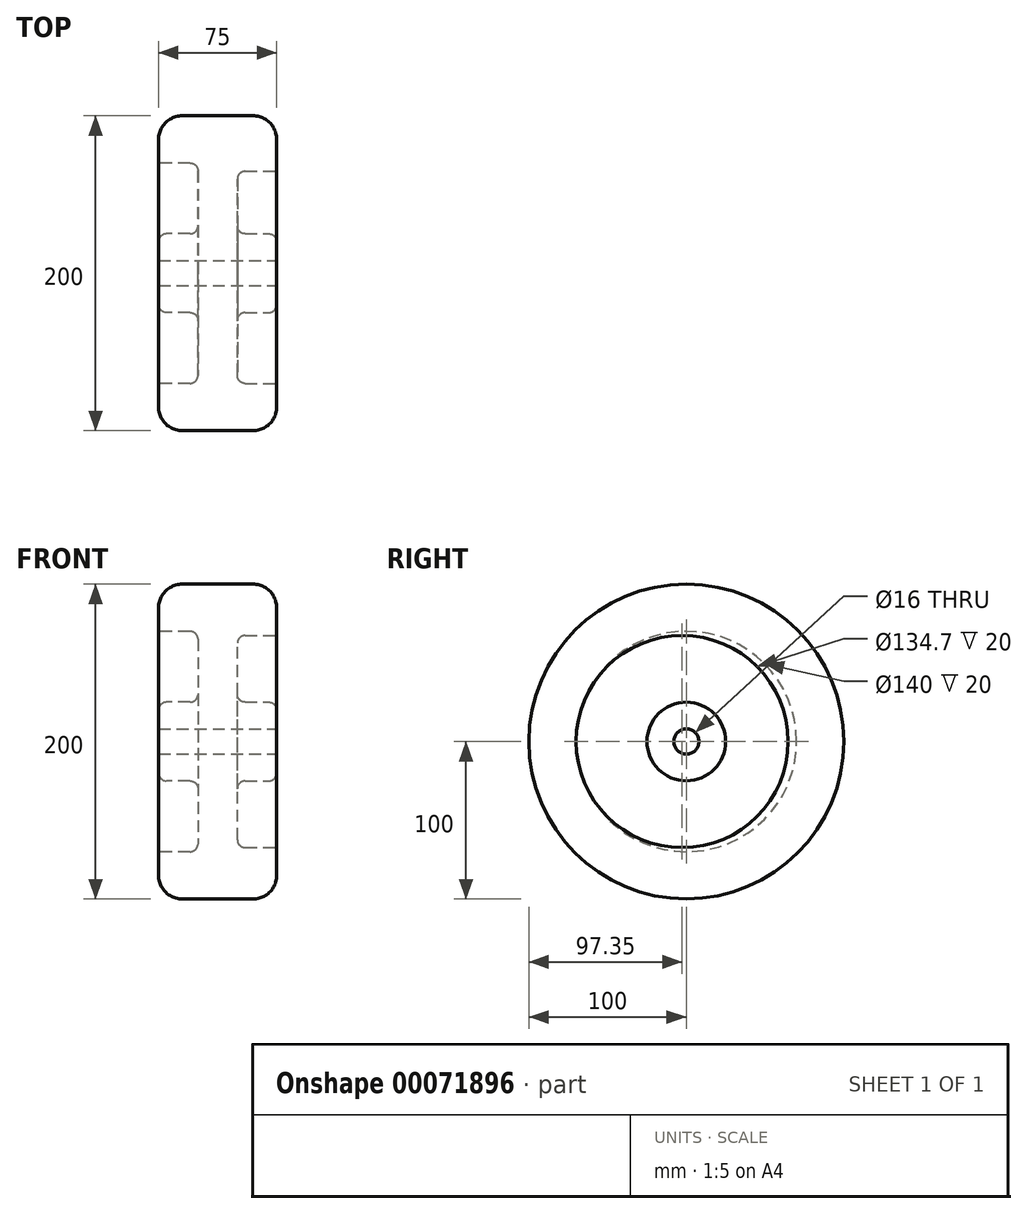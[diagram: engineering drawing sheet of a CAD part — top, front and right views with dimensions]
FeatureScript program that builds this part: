
annotation { "Feature Type Name" : "Feature", "Feature Type Description" : "" }
export const myFeature = defineFeature(function(context is Context, id is Id, definition is map)
    precondition{}
    {
        {
            var Q0;
            Q0=qCreatedBy(makeId("Right.planeOp"),FACE);
            var sketch = newSketch(context, id + "F0", { "sketchPlane" : qUnion([Q0])});
            skCircle(sketch, "E0", {"center": v(0, 0) * mm, "radius": 100 * mm});
            skSolve(sketch);
        }
        {
            var Q0;
            Q0 = qSketchRegion(id + "F0", true);
            extrude(context, id + "F1", {"entities" : qUnion([Q0]), "depth" : 75 * mm});
        }
        {
            var Q0;
            Q0=makeQuery(id+"F1.opExtrude","CAP_EDGE",EDGE,{"disambiguationData":[OSD([sQuery(id+"F0.wireOp",EDGE,"E0")])],"isStart":false});
            var Q1;
            Q1=makeQuery(id+"F1.opExtrude","CAP_EDGE",EDGE,{"disambiguationData":[OSD([sQuery(id+"F0.wireOp",EDGE,"E0")])],"isStart":true});
            fillet(context, id + "F2", {"entities" : qUnion([Q0, Q1]), "radius" : 15 * mm, "tangentPropagation" : true, "allowEdgeOverflow" : false});
        }
        {
            var Q0;
            Q0=makeQuery(id+"F1.opExtrude","CAP_FACE",FACE,{"disambiguationData":[OSD([sQuery(id+"F0.wireOp",EDGE,"E0")])],"isStart":false});
            var sketch = newSketch(context, id + "F3", { "sketchPlane" : qUnion([Q0])});
            skCircle(sketch, "E1", {"center": v(0, 0) * mm, "radius": 8 * mm});
            skSolve(sketch);
        }
        {
            var Q0;
            Q0 = qSketchRegion(id + "F3", true);
            extrude(context, id + "F4", {"entities" : qUnion([Q0]), "operationType" : NewBodyOperationType.REMOVE, "endBound" : BoundingType.THROUGH_ALL, "oppositeDirection" : true, "depth" : 25 * mm});
        }
        {
            var Q0;
            Q0=makeQuery(id+"F1.opExtrude","CAP_FACE",FACE,{"disambiguationData":[OSD([sQuery(id+"F0.wireOp",EDGE,"E0")])],"isStart":false});
            var sketch = newSketch(context, id + "F5", { "sketchPlane" : qUnion([Q0])});
            skCircle(sketch, "E2", {"center": v(0, 0) * mm, "radius": 25 * mm});
            skCircle(sketch, "E3", {"center": v(-2.65, 0) * mm, "radius": 67.35 * mm});
            skSolve(sketch);
        }
        {
            var Q0;
            Q0 = qSketchRegion(id + "F5", true);
            extrude(context, id + "F6", {"entities" : qUnion([Q0]), "operationType" : NewBodyOperationType.REMOVE, "oppositeDirection" : true, "depth" : 25 * mm});
        }
        {
            var Q0;
            Q0=makeQuery(id+"F1.opExtrude","CAP_FACE",FACE,{"disambiguationData":[OSD([sQuery(id+"F0.wireOp",EDGE,"E0")])],"isStart":true});
            var sketch = newSketch(context, id + "F7", { "sketchPlane" : qUnion([Q0])});
            skCircle(sketch, "E4", {"center": v(0, 0) * mm, "radius": 25 * mm});
            skCircle(sketch, "E5", {"center": v(0, 0) * mm, "radius": 70 * mm});
            skSolve(sketch);
        }
        {
            var Q0;
            Q0 = qSketchRegion(id + "F7", true);
            extrude(context, id + "F8", {"entities" : qUnion([Q0]), "operationType" : NewBodyOperationType.REMOVE, "oppositeDirection" : true, "depth" : 25 * mm});
        }
        {
            var Q0;
            Q0=makeQuery(id+"F6.boolean.opBoolean","COPY",EDGE,{"derivedFrom":makeQuery(id+"F6.opExtrude","CAP_EDGE",EDGE,{"disambiguationData":[OSD([sQuery(id+"F5.wireOp",EDGE,"E3")])],"isStart":true})});
            var Q1;
            Q1=makeQuery(id+"F6.boolean.opBoolean","COPY",EDGE,{"derivedFrom":makeQuery(id+"F6.opExtrude","CAP_EDGE",EDGE,{"disambiguationData":[OSD([sQuery(id+"F5.wireOp",EDGE,"E3")])],"isStart":false})});
            var Q2;
            Q2=makeQuery(id+"F6.boolean.opBoolean","COPY",EDGE,{"derivedFrom":makeQuery(id+"F6.opExtrude","CAP_EDGE",EDGE,{"disambiguationData":[OSD([sQuery(id+"F5.wireOp",EDGE,"E2")])],"isStart":false})});
            var Q3;
            Q3=makeQuery(id+"F6.boolean.opBoolean","COPY",EDGE,{"derivedFrom":makeQuery(id+"F6.opExtrude","CAP_EDGE",EDGE,{"disambiguationData":[OSD([sQuery(id+"F5.wireOp",EDGE,"E2")])],"isStart":true})});
            var Q4;
            Q4=makeQuery(id+"F8.boolean.opBoolean","COPY",EDGE,{"derivedFrom":makeQuery(id+"F8.opExtrude","CAP_EDGE",EDGE,{"disambiguationData":[OSD([sQuery(id+"F7.wireOp",EDGE,"E5")])],"isStart":true})});
            var Q5;
            Q5=makeQuery(id+"F8.boolean.opBoolean","COPY",EDGE,{"derivedFrom":makeQuery(id+"F8.opExtrude","CAP_EDGE",EDGE,{"disambiguationData":[OSD([sQuery(id+"F7.wireOp",EDGE,"E5")])],"isStart":false})});
            var Q6;
            Q6=makeQuery(id+"F8.boolean.opBoolean","COPY",EDGE,{"derivedFrom":makeQuery(id+"F8.opExtrude","CAP_EDGE",EDGE,{"disambiguationData":[OSD([sQuery(id+"F7.wireOp",EDGE,"E4")])],"isStart":false})});
            var Q7;
            Q7=makeQuery(id+"F8.boolean.opBoolean","COPY",EDGE,{"derivedFrom":makeQuery(id+"F8.opExtrude","CAP_EDGE",EDGE,{"disambiguationData":[OSD([sQuery(id+"F7.wireOp",EDGE,"E4")])],"isStart":true})});
            fillet(context, id + "F9", {"entities" : qUnion([Q0, Q1, Q2, Q3, Q4, Q5, Q6, Q7]), "radius" : 5 * mm, "tangentPropagation" : true, "allowEdgeOverflow" : false});
        }
    });
